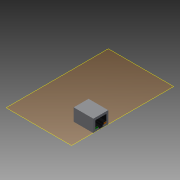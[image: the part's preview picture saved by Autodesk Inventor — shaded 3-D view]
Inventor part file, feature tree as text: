
AUTODESK INVENTOR PART (.ipt)
format: ipt  version: 2013 SP2 (Build 170200200, 200)  size: 138,752 bytes
history: native  units: mm
features: extrude x3, sketch x3, plane x1
ambient origin geometry x8: Origin, YZ Plane, XZ Plane, XY Plane, X Axis, Y Axis, Z Axis, Center Point
bodies: Solid1 (feature_tree)
feature tree (7):
  plane  "Work Plane1"
  extrude  "Extrusion1"  Depth=16.0mm
  extrude  "Extrusion2"  Depth=2.0mm
  extrude  "Extrusion3"  Depth=2.5mm
  sketch  "Sketch1"  dims[d0=21.2mm d2=16.0mm]
  sketch  "Sketch2"  dims[d3=13.4mm d4=0.0mm d5=2.0mm]
  sketch  "Sketch3"  dims[d6=2.0mm d7=2.5mm d8=5.0mm d9=6.0mm d10=1.0mm d11=2.5mm d12=4.3mm d13=11.5mm d14=0.0mm d15=0.2mm d16=0.2mm d17=0.2mm d18=0.2mm d19=0.2mm d20=0.0mm]
